# Revit family: NLRS_57_AIR_UN_linear-ceiling-grill-srxrxOx_supply_LT_sacs
name_source: partatom
category: Air Terminals
units: mm (PartAtom-declared; Revit-internal decimal feet)

## family parameters
Always vertical = Yes
Cut with Voids When Loaded = No
Part Type = Normal
Room Calculation Point = No
Round Connector Dimension = Use Diameter
Shared = No
Work Plane-Based = No

## types (2) — shared parameters
Assembly Code = 57.00
Default Elevation = 2700 mm  [stored 8.85827 ft]
Description = Solid Air Lineair Grill
Manufacturer = Solid Air Climate Solutions
Max Flow = 0.0 L/s
Min Flow = 0.0 L/s
Model = STxR linear grill, no plenum
NLRS_C_content_datum_gewijzigd = 11-03-2024
NLRS_C_content_provider = Solid Air Climate Solutions
NLRS_C_content_versie = 2.21.01
NLRS_C_description = Solid Air Lineair Grill
SACS_Data_Hidden = SRORxOx
SACS_Dummy = 1
Type Comments = Grill without plenum
URL = https://solid-air.nl

## per-type parameters (varying)
| type | SACS_Base_Index |
| 1 slot | 1 |
| 2-slot | 2 |

note: [stored X ft] marks values corroborated as IEEE doubles in the binary element streams (Revit-internal decimal feet)

## geometry (parser evidence)
native form markers: Sweep x17
no freeform markers — native parametric forms only
